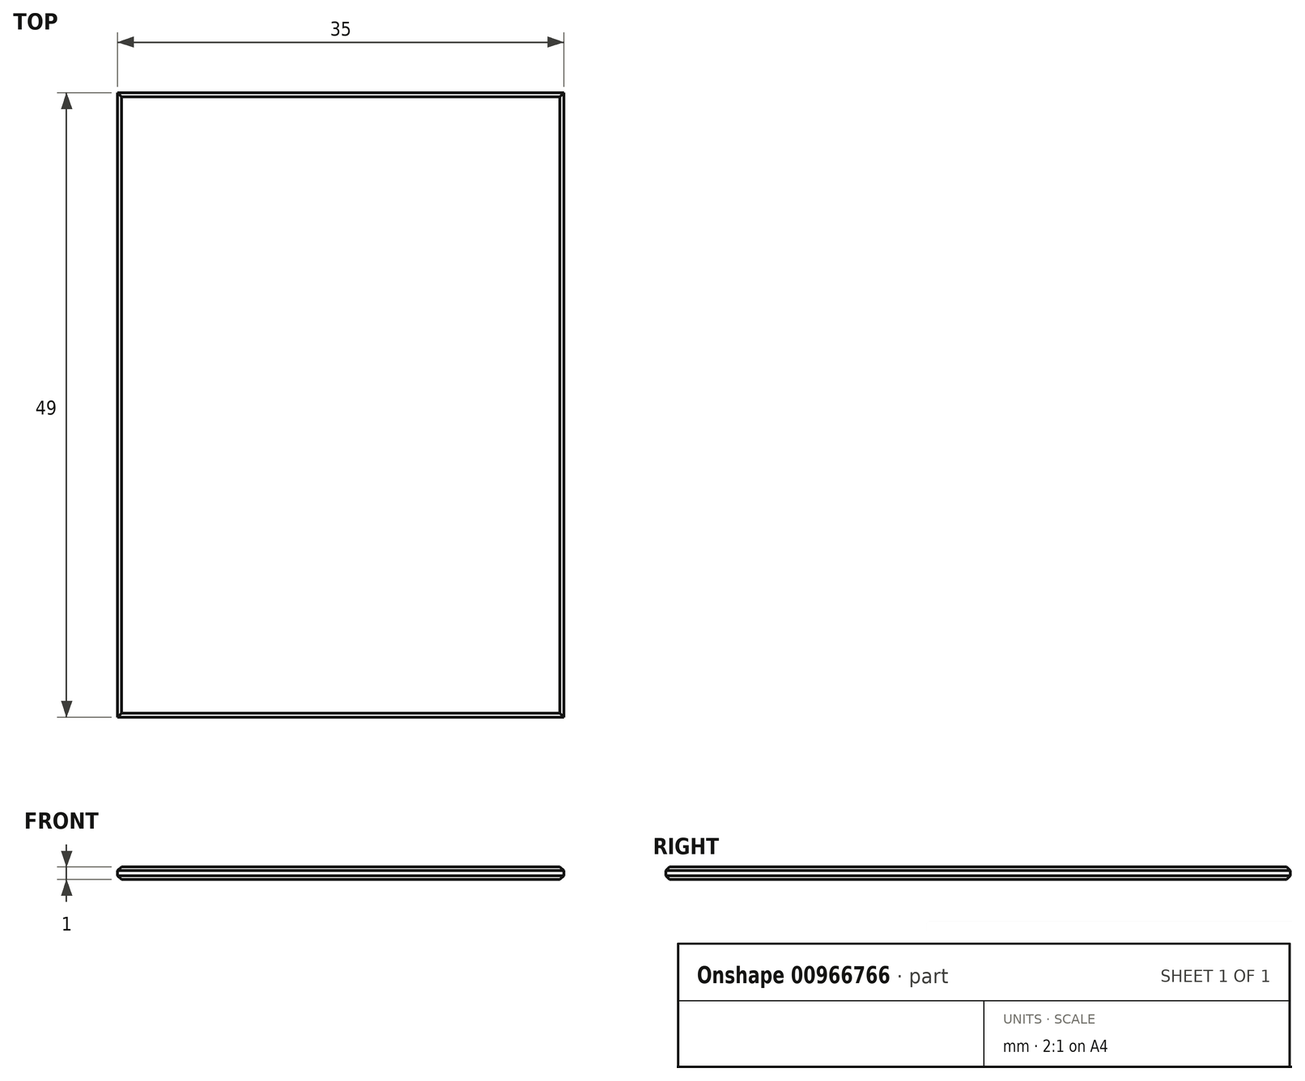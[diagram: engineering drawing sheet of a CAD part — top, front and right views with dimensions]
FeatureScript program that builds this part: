
annotation { "Feature Type Name" : "Feature", "Feature Type Description" : "" }
export const myFeature = defineFeature(function(context is Context, id is Id, definition is map)
    precondition{}
    {
        {
            var Q0;
            Q0=qCreatedBy(makeId("Top.planeOp"),FACE);
            var sketch = newSketch(context, id + "F0", { "sketchPlane" : qUnion([Q0])});
            skLineSegment(sketch, "E0.bottom", {"start": v(0, 0) * mm, "end": v(35, 0) * mm});
            skLineSegment(sketch, "E0.top", {"start": v(0, -49) * mm, "end": v(35, -49) * mm});
            skLineSegment(sketch, "E0.left", {"start": v(0, 0) * mm, "end": v(0, -49) * mm});
            skLineSegment(sketch, "E0.right", {"start": v(35, 0) * mm, "end": v(35, -49) * mm});
            skSolve(sketch);
        }
        {
            var Q0;
            Q0 = qSketchRegion(id + "F0", true);
            extrude(context, id + "F1", {"entities" : qUnion([Q0]), "depth" : 1 * mm, "offsetDistance" : 25 * mm});
        }
        {
            var Q0;
            Q0=makeQuery(id+"F1.opExtrude","CAP_FACE",FACE,{"disambiguationData":[OSD([sQuery(id+"F0.wireOp",EDGE,"E0.bottom"),sQuery(id+"F0.wireOp",EDGE,"E0.top"),sQuery(id+"F0.wireOp",EDGE,"E0.left"),sQuery(id+"F0.wireOp",EDGE,"E0.right")])],"isStart":false});
            var Q1;
            Q1=makeQuery(id+"F1.opExtrude","CAP_FACE",FACE,{"disambiguationData":[OSD([sQuery(id+"F0.wireOp",EDGE,"E0.bottom"),sQuery(id+"F0.wireOp",EDGE,"E0.top"),sQuery(id+"F0.wireOp",EDGE,"E0.left"),sQuery(id+"F0.wireOp",EDGE,"E0.right")])],"isStart":true});
            chamfer(context, id + "F2", {"entities" : qUnion([Q0, Q1]), "width" : 0.3 * mm, "tangentPropagation" : true});
        }
    });
